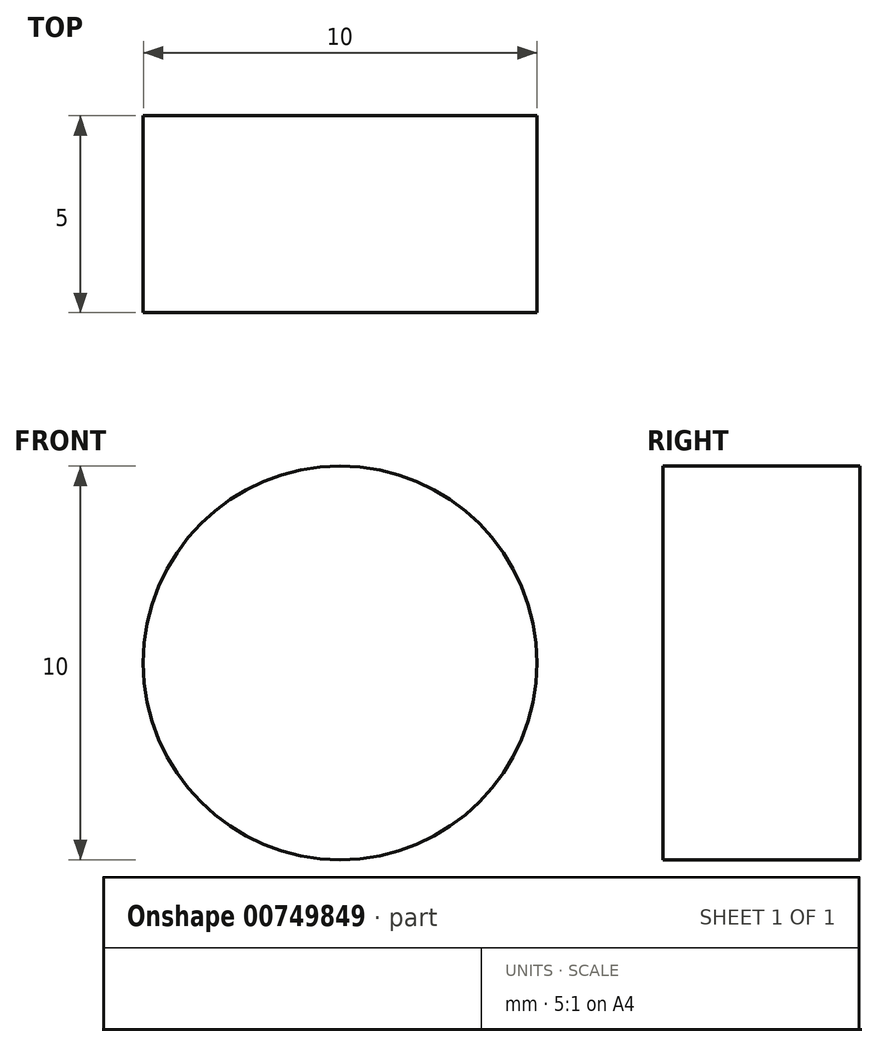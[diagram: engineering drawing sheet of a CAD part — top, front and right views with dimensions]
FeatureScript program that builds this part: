
annotation { "Feature Type Name" : "Feature", "Feature Type Description" : "" }
export const myFeature = defineFeature(function(context is Context, id is Id, definition is map)
    precondition{}
    {
        {
            var Q0;
            Q0=qCreatedBy(makeId("Front.planeOp"),FACE);
            var sketch = newSketch(context, id + "F0", { "sketchPlane" : qUnion([Q0])});
            skCircle(sketch, "E0", {"center": v(-62.03, 59.44) * mm, "radius": 5 * mm});
            skSolve(sketch);
        }
        {
            var Q0;
            Q0 = qSketchRegion(id + "F0", true);
            extrude(context, id + "F1", {"entities" : qUnion([Q0]), "depth" : 5 * mm, "offsetDistance" : 25 * mm});
        }
    });
